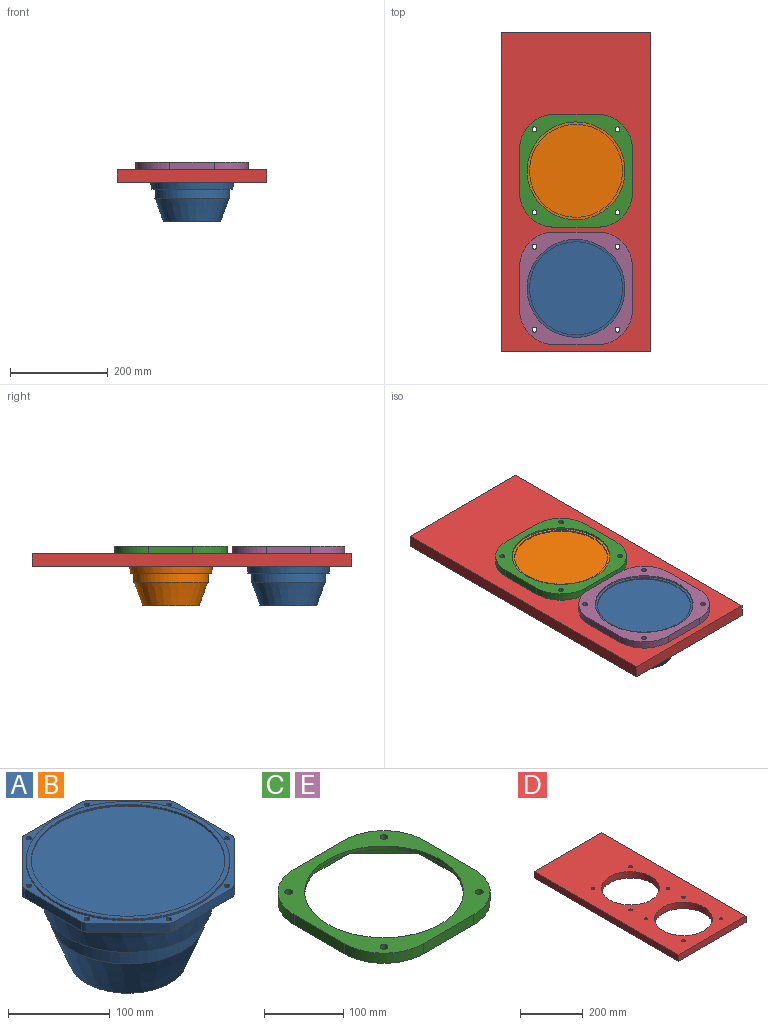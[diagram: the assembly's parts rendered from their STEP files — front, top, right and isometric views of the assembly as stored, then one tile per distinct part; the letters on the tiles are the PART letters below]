
ASSEMBLY  parts=5 mates=4
PART A: 35 faces, bbox 207.9x207.9x118.7 mm
  f0: cone r=83.17mm half-angle=10.6deg, axis (0,0,1), area 21716.7mm2, adj f1,f30
  f1: plane 166.34x166.34mm, normal (0,0,-1), area 3584.3mm2, adj f0,f2
  f2: cylinder r=76mm len=152mm, axis (0,0,1), area 9076.4mm2, adj f1,f3
  f3: cone r=57.9mm half-angle=20.7deg, axis (0,0,1), area 21528.4mm2, adj f2,f4
  f4: plane 115.81x115.81mm, normal (0,0,-1), area 10533.6mm2, adj f3
  f5: plane 79.9x10.7mm, normal (1,0,0), area 854.9mm2, adj f6,f21,f29,f30
  f6: cylinder r=7.5mm len=10.7mm, axis (0,0,-1), area 63mm2, adj f5,f7,f29,f30
  f7: plane 56.5x56.5mm, normal (0.71,0.71,0), area 854.9mm2, adj f6,f8,f29,f30
  f8: cylinder r=7.5mm len=10.7mm, axis (0,0,-1), area 63mm2, adj f7,f9,f29,f30
  f9: plane 79.9x10.7mm, normal (0,1,0), area 854.9mm2, adj f8,f10,f29,f30
  f10: cylinder r=7.5mm len=10.7mm, axis (0,0,-1), area 63mm2, adj f9,f11,f29,f30
  f11: plane 56.5x56.5mm, normal (-0.71,0.71,0), area 854.9mm2, adj f10,f12,f29,f30
  f12: cylinder r=7.5mm len=10.7mm, axis (0,0,-1), area 63mm2, adj f11,f13,f29,f30
  f13: plane 79.9x10.7mm, normal (-1,0,0), area 854.9mm2, adj f12,f14,f29,f30
  f14: cylinder r=7.5mm len=10.7mm, axis (0,0,-1), area 63mm2, adj f13,f15,f29,f30
  f15: plane 56.5x56.5mm, normal (-0.71,-0.71,0), area 854.9mm2, adj f14,f16,f29,f30
  f16: cylinder r=7.5mm len=10.7mm, axis (0,0,-1), area 63mm2, adj f15,f17,f29,f30
  f17: plane 79.9x10.7mm, normal (0,-1,0), area 854.9mm2, adj f16,f18,f29,f30
  f18: cylinder r=7.5mm len=10.7mm, axis (0,0,-1), area 63mm2, adj f17,f19,f29,f30
  f19: plane 56.5x56.5mm, normal (0.71,-0.71,0), area 854.9mm2, adj f18,f21,f29,f30
  f20: cylinder r=2.75mm len=10.7mm, axis (0,0,-1), area 184.9mm2, adj f29,f30
  f21: cylinder r=7.5mm len=10.7mm, axis (0,0,-1), area 63mm2, adj f5,f19,f29,f30
  f22: cylinder r=2.75mm len=10.7mm, axis (0,0,-1), area 184.9mm2, adj f29,f30
  f23: cylinder r=2.75mm len=10.7mm, axis (0,0,-1), area 184.9mm2, adj f29,f30
  f24: cylinder r=2.75mm len=10.7mm, axis (0,0,-1), area 184.9mm2, adj f29,f30
  f25: cylinder r=2.75mm len=10.7mm, axis (0,0,-1), area 184.9mm2, adj f29,f30
  f26: cylinder r=2.75mm len=10.7mm, axis (0,0,-1), area 184.9mm2, adj f29,f30
  f27: cylinder r=2.75mm len=10.7mm, axis (0,0,-1), area 184.9mm2, adj f29,f30
  f28: cylinder r=2.75mm len=10.7mm, axis (0,0,-1), area 184.9mm2, adj f29,f30
  f29: plane 207.9x207.9mm, normal (0,0,1), area 4190.9mm2, adj f5,f6,f7,f8,f9,f10,f11,f12
  f30: plane 207.9x207.9mm, normal (0,0,-1), area 9876.4mm2, adj f0,f5,f6,f7,f8,f9,f10,f11
  f31: cylinder r=95mm len=190mm, axis (0,0,-1), area 1193.8mm2, adj f33,f34
  f32: cylinder r=100mm len=200mm, axis (0,0,-1), area 1256.6mm2, adj f29,f33
  f33: plane 200x200mm, normal (0,0,1), area 3063.1mm2, adj f31,f32
  f34: plane 190x190mm, normal (0,0,1), area 28352.9mm2, adj f31
PART B: same geometry as A
PART C: 32 faces, bbox 230x230x15.7 mm
  f0: plane 230x230mm, normal (0,0,-1), area 11191.6mm2, adj f1,f2,f3,f4,f5,f6,f7,f8
  f1: cylinder r=70mm len=70mm, axis (0,0,-1), area 1726.3mm2, adj f0,f2,f9,f14
  f2: plane 90x15.7mm, normal (0,-1,0), area 1413mm2, adj f0,f1,f3,f14
  f3: cylinder r=70mm len=70mm, axis (0,0,-1), area 1726.3mm2, adj f0,f2,f4,f14
  f4: plane 90x15.7mm, normal (1,0,0), area 1413mm2, adj f0,f3,f5,f14
  f5: cylinder r=70mm len=70mm, axis (0,0,-1), area 1726.3mm2, adj f0,f4,f6,f14
  f6: plane 90x15.7mm, normal (0,1,0), area 1413mm2, adj f0,f5,f7,f14
  f7: cylinder r=70mm len=70mm, axis (0,0,-1), area 1726.3mm2, adj f0,f6,f9,f14
  f8: cylinder r=5mm len=15.7mm, axis (0,0,-1), area 493.2mm2, adj f0,f14
  f9: plane 90x15.7mm, normal (-1,0,0), area 1413mm2, adj f0,f1,f7,f14
  f10: cylinder r=100mm len=200mm, axis (0,0,-1), area 3141.6mm2, adj f14,f31
  f11: cylinder r=5mm len=15.7mm, axis (0,0,-1), area 493.2mm2, adj f0,f14
  f12: cylinder r=5mm len=15.7mm, axis (0,0,-1), area 493.2mm2, adj f0,f14
  f13: cylinder r=5mm len=15.7mm, axis (0,0,-1), area 493.2mm2, adj f0,f14
  f14: plane 230x230mm, normal (0,0,1), area 16963.7mm2, adj f1,f2,f3,f4,f5,f6,f7,f8
  f15: plane 81.56x10.7mm, normal (-1,0,0), area 872.7mm2, adj f0,f16,f30,f31
  f16: cylinder r=7.5mm len=10.7mm, axis (0,0,-1), area 63mm2, adj f0,f15,f17,f31
  f17: plane 57.67x57.67mm, normal (-0.71,-0.71,0), area 872.7mm2, adj f0,f16,f18,f31
  f18: cylinder r=7.5mm len=10.7mm, axis (0,0,-1), area 63mm2, adj f0,f17,f19,f31
  f19: plane 81.56x10.7mm, normal (0,-1,0), area 872.7mm2, adj f0,f18,f20,f31
  f20: cylinder r=7.5mm len=10.7mm, axis (0,0,-1), area 63mm2, adj f0,f19,f21,f31
  f21: plane 57.67x57.67mm, normal (0.71,-0.71,0), area 872.7mm2, adj f0,f20,f22,f31
  f22: cylinder r=7.5mm len=10.7mm, axis (0,0,-1), area 63mm2, adj f0,f21,f23,f31
  f23: plane 81.56x10.7mm, normal (1,0,0), area 872.7mm2, adj f0,f22,f24,f31
  f24: cylinder r=7.5mm len=10.7mm, axis (0,0,-1), area 63mm2, adj f0,f23,f25,f31
  f25: plane 57.67x57.67mm, normal (0.71,0.71,0), area 872.7mm2, adj f0,f24,f26,f31
  f26: cylinder r=7.5mm len=10.7mm, axis (0,0,-1), area 63mm2, adj f0,f25,f27,f31
  f27: plane 81.56x10.7mm, normal (0,1,0), area 872.7mm2, adj f0,f26,f28,f31
  f28: cylinder r=7.5mm len=10.7mm, axis (0,0,-1), area 63mm2, adj f0,f27,f29,f31
  f29: plane 57.67x57.67mm, normal (-0.71,0.71,0), area 872.7mm2, adj f0,f28,f30,f31
  f30: cylinder r=7.5mm len=10.7mm, axis (0,0,-1), area 63mm2, adj f0,f15,f29,f31
  f31: plane 211.9x211.9mm, normal (0,0,-1), area 5772.1mm2, adj f10,f15,f16,f17,f18,f19,f20,f21
PART D: 16 faces, bbox 305.7x653.6x25 mm
  f0: plane 305.69x25mm, normal (0,-1,0), area 7642.3mm2, adj f1,f5,f14,f15
  f1: plane 653.62x25mm, normal (1,0,0), area 16340.6mm2, adj f0,f2,f14,f15
  f2: plane 305.69x25mm, normal (0,1,0), area 7642.3mm2, adj f1,f5,f14,f15
  f3: cylinder r=5.5mm len=25mm, axis (0,0,-1), area 863.9mm2, adj f14,f15
  f4: cylinder r=5.5mm len=25mm, axis (0,0,-1), area 863.9mm2, adj f14,f15
  f5: plane 653.62x25mm, normal (-1,0,0), area 16340.6mm2, adj f0,f2,f14,f15
  f6: cylinder r=92.5mm len=185mm, axis (0,0,-1), area 14529.9mm2, adj f14,f15
  f7: cylinder r=5.5mm len=25mm, axis (0,0,-1), area 863.9mm2, adj f14,f15
  f8: cylinder r=5.5mm len=25mm, axis (0,0,-1), area 863.9mm2, adj f14,f15
  f9: cylinder r=5.5mm len=25mm, axis (0,0,-1), area 863.9mm2, adj f14,f15
  f10: cylinder r=92.5mm len=185mm, axis (0,0,-1), area 14529.9mm2, adj f14,f15
  f11: cylinder r=5.5mm len=25mm, axis (0,0,-1), area 863.9mm2, adj f14,f15
  f12: cylinder r=5.5mm len=25mm, axis (0,0,-1), area 863.9mm2, adj f14,f15
  f13: cylinder r=5.5mm len=25mm, axis (0,0,-1), area 863.9mm2, adj f14,f15
  f14: plane 653.62x305.69mm, normal (0,0,1), area 145286mm2, adj f0,f1,f2,f3,f4,f5,f6,f7
  f15: plane 653.62x305.69mm, normal (0,0,-1), area 145286mm2, adj f0,f1,f2,f3,f4,f5,f6,f7
PART E: same geometry as C
PLACE A t=(-467.48,-427.75,-180.01)mm
PLACE B t=(-467.48,-187.75,-180.01)mm
PLACE C t=(-596.68,296.69,-74.01)mm
PLACE D t=(-165.46,308.05,-99.01)mm
PLACE E t=(-596.68,56.69,-74.01)mm
MATE fastened B.f0 <-> D.f10  axis (0,0,-1) through (-318.3,-187.75,-74.01)mm
MATE fastened E.f12 <-> D.f4  axis (0,0,-1) through (-403.15,-512.6,-74.01)mm
MATE fastened C.f12 <-> D.f12  axis (0,0,-1) through (-403.15,-272.6,-74.01)mm
MATE fastened A.f0 <-> D.f6  axis (0,0,-1) through (-318.3,-427.75,-74.01)mm
